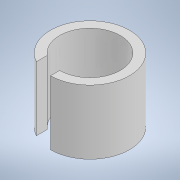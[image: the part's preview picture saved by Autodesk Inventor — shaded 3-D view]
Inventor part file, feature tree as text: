
AUTODESK INVENTOR PART (.ipt)
format: ipt  version: 2022 (Build 260153000, 153)  size: 103,936 bytes
history: native  units: in
note: dims shown in document units (in); Inventor stores cm internally (conversion verified against a paired STEP export)
features: extrude x1, sketch x1
ambient origin geometry x8: Origin, YZ Plane, XZ Plane, XY Plane, X Axis, Y Axis, Z Axis, Center Point
bodies: Solid1 (feature_tree)
feature tree (2):
  extrude  "Extrusion1"  Depth=0.075in
  sketch  "Sketch1"  dims[d0=0.2362in d1=0.3071in d2=0.25in d3=0.0in d4=0.075in d5=0.075in]
